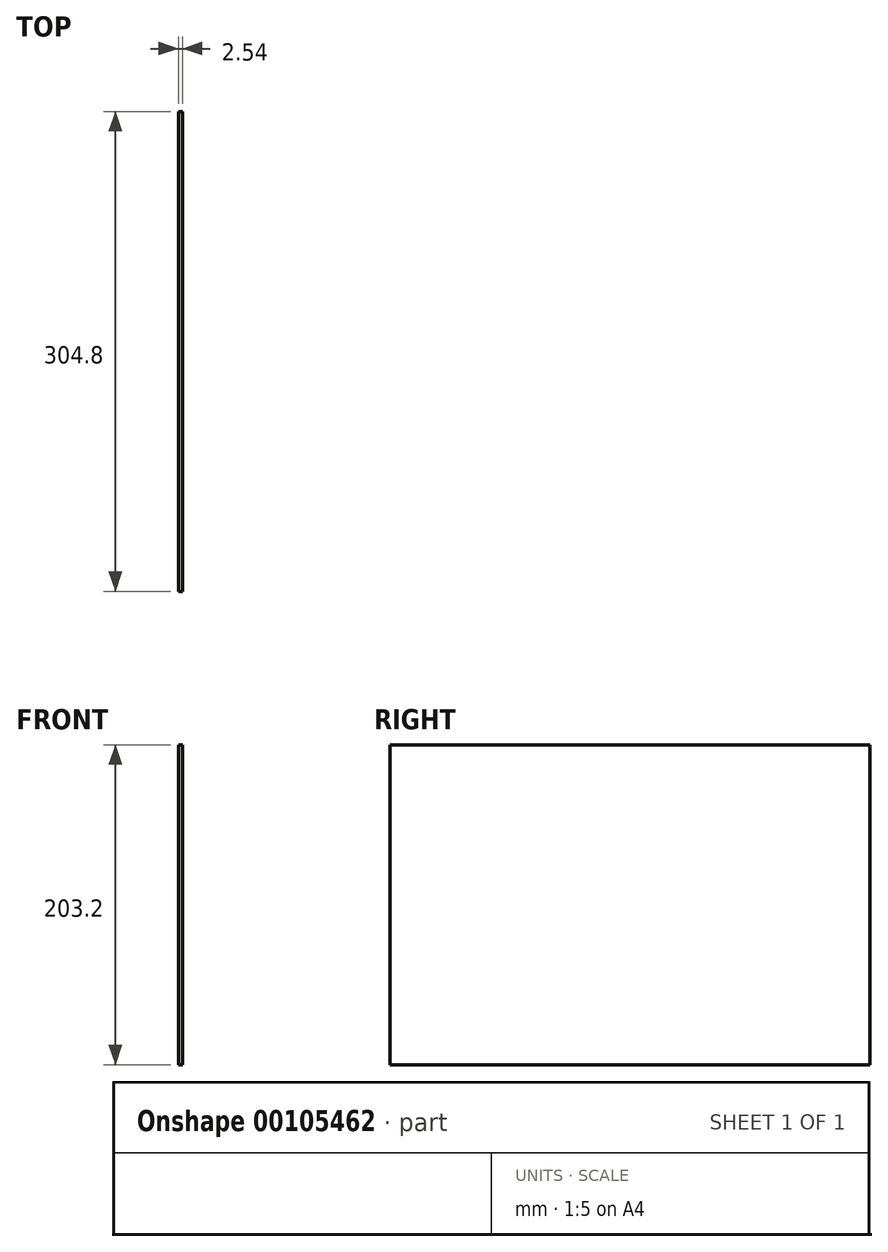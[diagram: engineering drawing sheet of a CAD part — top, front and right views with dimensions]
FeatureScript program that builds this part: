
annotation { "Feature Type Name" : "Feature", "Feature Type Description" : "" }
export const myFeature = defineFeature(function(context is Context, id is Id, definition is map)
    precondition{}
    {
        {
            var Q0;
            Q0=qCreatedBy(makeId("Front.planeOp"),FACE);
            var sketch = newSketch(context, id + "F0", { "sketchPlane" : qUnion([Q0])});
            skLineSegment(sketch, "E0.bottom", {"start": v(-152.4, 101.6) * mm, "end": v(152.4, 101.6) * mm});
            skLineSegment(sketch, "E0.top", {"start": v(-152.4, -101.6) * mm, "end": v(152.4, -101.6) * mm});
            skLineSegment(sketch, "E0.left", {"start": v(-152.4, 101.6) * mm, "end": v(-152.4, -101.6) * mm});
            skLineSegment(sketch, "E0.right", {"start": v(152.4, 101.6) * mm, "end": v(152.4, -101.6) * mm});
            skPoint(sketch, "E0.middle", {"position": v(0, 0) * mm});
            skSolve(sketch);
        }
        {
            var Q0;
            Q0=makeQuery(id+"F0.imprint","IMPRINT",FACE,{"disambiguationData":[TD([[makeQuery(id+"F0.imprint","IMPRINT",EDGE,{"derivedFrom":sQuery(id+"F0.wireOp",EDGE,"E0.bottom")}),-1.0]])]});
            extrude(context, id + "F1", {"entities" : qUnion([Q0]), "depth" : 2.54 * mm});
        }
        {
            var Q0;
            Q0=makeQuery(id+"F1.opExtrude","SWEPT_BODY",BODY,{"disambiguationData":[OSD([sQuery(id+"F0.wireOp",EDGE,"E0.bottom"),sQuery(id+"F0.wireOp",EDGE,"E0.top"),sQuery(id+"F0.wireOp",EDGE,"E0.left"),sQuery(id+"F0.wireOp",EDGE,"E0.right")])]});
            var Q1;
            Q1=makeQuery(id+"F1.opExtrude","CAP_EDGE",EDGE,{"disambiguationData":[OSD([sQuery(id+"F0.wireOp",EDGE,"E0.left")])],"isStart":false});
            transform(context, id + "F2", {"entities" : qUnion([Q0]), "transformType" : TransformType.ROTATION, "transformAxis" : qUnion([Q1]), "angle" : 90 * degree, "makeCopy" : false});
        }
    });
